# Revit family: Accessory-Shower-Foot_Ledge-KOHLER-K-26306T
name_source: partatom
category: Specialty Equipment
revit_build: Autodesk Revit 2017 (Build: 20160225_1515(x64)
units: mm (PartAtom-declared; Revit-internal decimal feet)

## family parameters
Cut with Voids When Loaded = No
Host = Face
OmniClass Number = 23.31.25.00
OmniClass Title = Toilet and Bath Specialties
Part Type = Normal
Room Calculation Point = No
Round Connector Dimension = Use Diameter
Shared = No

## types (7) — shared parameters
ADA Compliant = No
Assembly Code = C1030200
Date Modified = 02/05/2021
Default Elevation = 15"
Description = FOOT LEDGE, INTEGRATED WITH EXPOSED SHOWER
Height = 3 5/16"
Length = 5 1/16"
Manufacturer = KOHLER Co.
Master Format 2014 = 10 28 00
Master Format 2014 Name = Toilet, Bath, and Laundry Accessories
Material = Plastic
URL = http://www.kohler.com.cn
WaterSense Certified = No
Width = 11 13/16"

## per-type parameters (varying)
| type | Finish | Model | Type |
| CP-Polished Chrome | Kohler-Plastic-CP-Polished_Chrome | K-26306T-CP | 1 |
| BN-Vibrant Brushed Nickel | KOHLER-Plastic-BN-Vibrant_Brushed_Nickel | K-26306T-BN | 2 |
| BL-Matte Black | KOHLER-Plastic-BL-Matte_Black | K-26306T-BL | 3 |
| 2MB-Vibrant Brushed Moderne Brass | KOHLER-Plastic-2MB-Vibrant_Brushed_Moderne_Brass | K-26306T-2MB | 4 |
| AF-Vibrant French Gold | KOHLER-Plastic-AF-Vibrant_French_Gold | K-26306T-AF | 5 |
| RGD-Rose Gold | Kohler-Plastic-RGD-Rose_Gold | K-26306T-RGD | 6 |
| SN-Vibrant Polished Nickel | KOHLER-Plasticl-SN-Vibrant_Polished_Nickel | K-26306T-SN | 7 |

## geometry (parser evidence)
native form markers: Sweep x5
no freeform markers — native parametric forms only
